# Revit family: KEUCO_51688010300
name_source: partatom
category: Sonderausstattung
revit_build: Autodesk Revit 2016 (Build: 20150220_1215(x64)
units: mm (PartAtom-declared; Revit-internal decimal feet)

## family parameters
Arbeitsebenenbasiert = Nein
Beim Laden mit Abzugskörper schneiden = Nein
Bemaßung runder Anschluss = Durchmesser verwenden
Gemeinsam genutzt = Nein
Immer vertikal = Ja
OmniClass-Nummer = 23.45.05.00
Raumberechnungspunkt = Nein
Teiletyp = Normal

## types (2) — shared parameters
Beschreibung = für Wandanschluß G 1/2, mit runder Rosette,
Möglichkeit der Ausrichtung zur Wand (90° ± 2°) und
zum Wandanschluß (90° ± 5°)
Gewicht = 1.37
Hersteller = KEUCO
Kategorie = ARM
KnopfUnten = Ja
KreisBase = Ja
Preisgruppe = 1
Serie = Elegance
URL = https://www.keuco.com
Verwendung = DU / WA
ViereckBase = Nein

## per-type parameters (varying)
| type | Armelänge | Ausschreibungstext |
| 51688010400 | 450 mm  [stored 1.47638 ft] | KEUCO Brausearm für Wandanschluss 51688010400 
Hochglanzverchromter Brausearm für Wandanschluss
G 1/2 Zoll, mit runder Rosette, 
Durchmesser der Rosette 80 mm,
Möglichkeit zur Ausrichtung zur Wand (90° ± 2°) und 
zum Wandanschluss (90° ± 5°),
Gesamtausladung:462 mm

Hinweis:
Passende UP Funktionseinheit
59547000170 |
| 51688010300 | 300 mm | KEUCO Brausearm für Wandanschluss 51688010300 
Hochglanzverchromter Brausearm für Wandanschluss
G 1/2 Zoll, mit runder Rosette, 
Durchmesser der Rosette 80 mm,
Möglichkeit zur Ausrichtung zur Wand (90° ± 2°) und 
zum Wandanschluss (90° ± 5°),
Gesamtausladung:312 mm

Hinweis:
Passende UP Funktionseinheit
59547000170 |

note: column(s) folded — value = type name in every type: Artikelnummer

note: [stored X ft] marks values corroborated as IEEE doubles in the binary element streams (Revit-internal decimal feet)

## geometry (parser evidence)
native form markers: Blend x2, Sweep x3
no freeform markers — native parametric forms only
